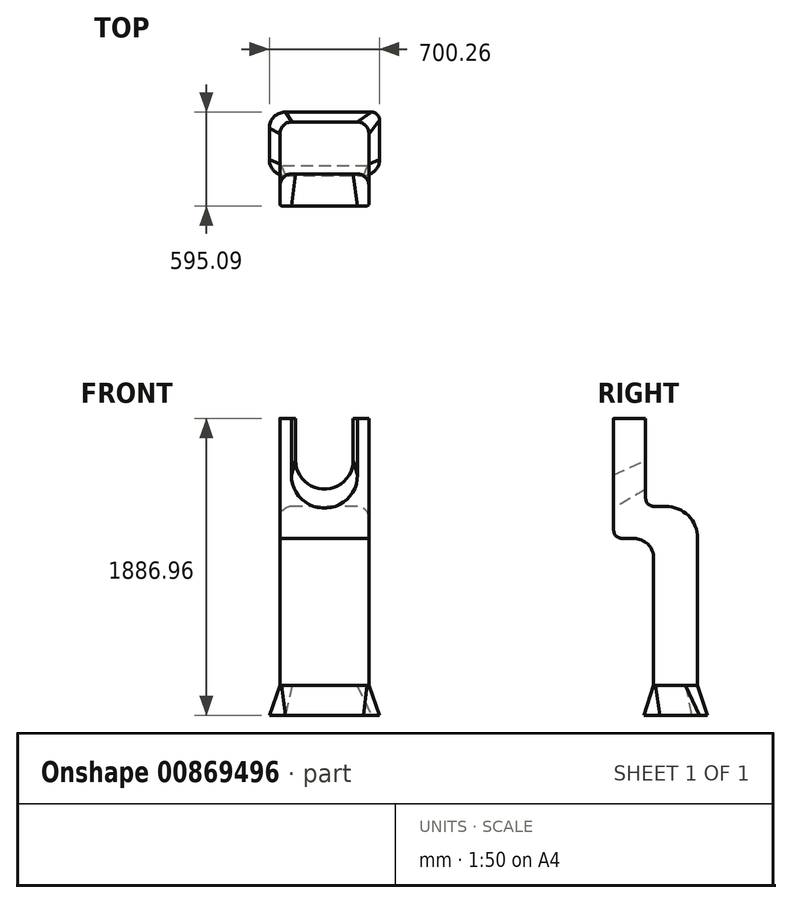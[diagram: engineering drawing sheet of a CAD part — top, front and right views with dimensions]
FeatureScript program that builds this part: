
annotation { "Feature Type Name" : "Feature", "Feature Type Description" : "" }
export const myFeature = defineFeature(function(context is Context, id is Id, definition is map)
    precondition{}
    {
        {
            var Q0;
            Q0=qCreatedBy(makeId("Right.planeOp"),FACE);
            var sketch = newSketch(context, id + "F0", { "sketchPlane" : qUnion([Q0])});
            skLineSegment(sketch, "E0", {"start": v(0, 690.62) * mm, "end": v(0, -1004.83) * mm, "construction": true});
            skSolve(sketch);
        }
        {
            var Q0;
            Q0=qCreatedBy(makeId("Right.planeOp"),FACE);
            var sketch = newSketch(context, id + "F1", { "sketchPlane" : qUnion([Q0])});
            skLineSegment(sketch, "E1", {"start": v(139.7, -1004.83) * mm, "end": v(-139.7, -1004.83) * mm});
            skLineSegment(sketch, "E2", {"start": v(-139.7, -1004.83) * mm, "end": v(-139.7, -198.38) * mm});
            skLineSegment(sketch, "E3", {"start": v(-266.7, -71.38) * mm, "end": v(-342.9, -71.38) * mm});
            skLineSegment(sketch, "E4", {"start": v(-393.7, -20.58) * mm, "end": v(-393.7, 690.62) * mm});
            skLineSegment(sketch, "E5.0", {"start": v(-190.5, 182.62) * mm, "end": v(-190.5, 690.62) * mm});
            skLineSegment(sketch, "E6.0", {"start": v(139.7, -1004.83) * mm, "end": v(139.7, -71.38) * mm});
            skLineSegment(sketch, "E7.0", {"start": v(-63.5, 131.82) * mm, "end": v(-139.7, 131.82) * mm});
            skPoint(sketch, "E8.visualSharp", {"position": v(-393.7, -71.38) * mm});
            skArc(sketch, "E8.filletArc", {"start": v(-393.7, -20.58) * mm, "mid": v(-378.82, -56.5) * mm, "end": v(-342.9, -71.38) * mm});
            skPoint(sketch, "E9.visualSharp", {"position": v(-190.5, 131.82) * mm});
            skArc(sketch, "E9.filletArc", {"start": v(-190.5, 182.62) * mm, "mid": v(-175.62, 146.7) * mm, "end": v(-139.7, 131.82) * mm});
            skPoint(sketch, "E10.visualSharp", {"position": v(-139.7, -71.38) * mm});
            skArc(sketch, "E10.filletArc", {"start": v(-139.7, -198.38) * mm, "mid": v(-176.9, -108.58) * mm, "end": v(-266.7, -71.38) * mm});
            skPoint(sketch, "E11.visualSharp", {"position": v(139.7, 131.82) * mm});
            skArc(sketch, "E11.filletArc", {"start": v(139.7, -71.38) * mm, "mid": v(80.18, 72.3) * mm, "end": v(-63.5, 131.82) * mm});
            skLineSegment(sketch, "E12", {"start": v(-393.7, 690.62) * mm, "end": v(-190.5, 690.62) * mm});
            skSolve(sketch);
        }
        {
            var Q0;
            Q0=makeQuery(id+"F1.imprint","IMPRINT",FACE,{"disambiguationData":[TD([[makeQuery(id+"F1.imprint","IMPRINT",EDGE,{"derivedFrom":sQuery(id+"F1.wireOp",EDGE,"E1")}),-1.0]])]});
            extrude(context, id + "F2", {"entities" : qUnion([Q0]), "depth" : 282.57 * mm, "offsetDistance" : 25.4 * mm, "hasSecondDirection" : true, "secondDirectionOppositeDirection" : true, "secondDirectionDepth" : 282.57 * mm});
        }
        {
            var Q0;
            Q0=qCreatedBy(makeId("Front.planeOp"),FACE);
            cPlane(context, id + "F3", {"entities" : qUnion([Q0]), "cplaneType" : CPlaneType.OFFSET, "offset" : 525.78 * mm, "width" : 152.4 * mm, "height" : 152.4 * mm});
        }
        {
            var Q0;
            Q0=qCreatedBy(makeId("Front.planeOp"),FACE);
            cPlane(context, id + "F4", {"entities" : qUnion([Q0]), "cplaneType" : CPlaneType.OFFSET, "offset" : 154.94 * mm, "width" : 152.4 * mm, "height" : 152.4 * mm});
        }
        {
            var Q0;
            Q0=qCreatedBy(id+"F4.planeOp",FACE);
            var sketch = newSketch(context, id + "F5", { "sketchPlane" : qUnion([Q0])});
            skArc(sketch, "E13", {"start": v(-177.8, 439.13) * mm, "mid": v(0, 261.33) * mm, "end": v(177.8, 439.13) * mm});
            skLineSegment(sketch, "E14", {"start": v(-177.8, 439.13) * mm, "end": v(-177.8, 864.72) * mm});
            skLineSegment(sketch, "E15", {"start": v(177.8, 439.13) * mm, "end": v(177.8, 864.72) * mm});
            skLineSegment(sketch, "E16", {"start": v(-177.8, 864.72) * mm, "end": v(177.8, 864.72) * mm});
            skSolve(sketch);
        }
        {
            var Q0;
            Q0=qCreatedBy(id+"F3.planeOp",FACE);
            var sketch = newSketch(context, id + "F6", { "sketchPlane" : qUnion([Q0])});
            skArc(sketch, "E17", {"start": v(-228.6, 270.81) * mm, "mid": v(0, 42.21) * mm, "end": v(228.6, 270.81) * mm});
            skLineSegment(sketch, "E18", {"start": v(-228.6, 270.81) * mm, "end": v(-228.6, 1000.47) * mm});
            skLineSegment(sketch, "E19", {"start": v(228.6, 270.81) * mm, "end": v(228.6, 1000.47) * mm});
            skLineSegment(sketch, "E20", {"start": v(-228.6, 1000.47) * mm, "end": v(228.6, 1000.47) * mm});
            skSolve(sketch);
        }
        {
            var Q1;
            Q1=makeQuery(id+"F6.imprint","IMPRINT",FACE,{"disambiguationData":[TD([[makeQuery(id+"F6.imprint","IMPRINT",EDGE,{"derivedFrom":sQuery(id+"F6.wireOp",EDGE,"E17")}),1.0]])]});
            var Q2;
            Q2=makeQuery(id+"F5.imprint","IMPRINT",FACE,{"disambiguationData":[TD([[makeQuery(id+"F5.imprint","IMPRINT",EDGE,{"derivedFrom":sQuery(id+"F5.wireOp",EDGE,"E13")}),1.0]])]});
            loft(context, id + "F7", {"operationType" : NewBodyOperationType.REMOVE, "sheetProfilesArray" : [{ "sheetProfileEntities" : qUnion([Q1]) }, { "sheetProfileEntities" : qUnion([Q2]) }]});
        }
        {
            var Q0;
            Q0=makeQuery(id+"F2.opExtrude","CAP_EDGE",EDGE,{"disambiguationData":[OSD([sQuery(id+"F1.wireOp",EDGE,"E4")])],"isStart":true});
            var Q1;
            Q1=makeQuery(id+"F2.opExtrude","CAP_EDGE",EDGE,{"disambiguationData":[OSD([sQuery(id+"F1.wireOp",EDGE,"E4")])],"isStart":false});
            fillet(context, id + "F8", {"entities" : qUnion([Q0, Q1]), "radius" : 11.43 * mm, "tangentPropagation" : true, "allowEdgeOverflow" : false});
        }
        {
            var Q0;
            Q0=makeQuery(id+"F2.opExtrude","CAP_EDGE",EDGE,{"disambiguationData":[OSD([sQuery(id+"F1.wireOp",EDGE,"E5.0")])],"isStart":true});
            var Q1;
            Q1=makeQuery(id+"F2.opExtrude","CAP_EDGE",EDGE,{"disambiguationData":[OSD([sQuery(id+"F1.wireOp",EDGE,"E5.0")])],"isStart":false});
            fillet(context, id + "F9", {"entities" : qUnion([Q0, Q1]), "radius" : 76.2 * mm, "tangentPropagation" : true, "allowEdgeOverflow" : false});
        }
        {
            var Q0;
            Q0=qCreatedBy(makeId("Top.planeOp"),FACE);
            cPlane(context, id + "F10", {"entities" : qUnion([Q0]), "cplaneType" : CPlaneType.OFFSET, "offset" : 1196.34 * mm, "oppositeDirection" : true, "width" : 152.4 * mm, "height" : 152.4 * mm});
        }
        {
            var Q0;
            Q0=qCreatedBy(id+"F10.planeOp",FACE);
            var sketch = newSketch(context, id + "F11", { "sketchPlane" : qUnion([Q0])});
            skLineSegment(sketch, "E21.bottom", {"start": v(-248.53, -201.4) * mm, "end": v(248.53, -201.4) * mm});
            skLineSegment(sketch, "E21.top", {"start": v(-248.53, 201.4) * mm, "end": v(299.33, 201.4) * mm});
            skLineSegment(sketch, "E21.left", {"start": v(-350.13, -99.8) * mm, "end": v(-350.13, 99.8) * mm});
            skLineSegment(sketch, "E21.right", {"start": v(350.13, -99.8) * mm, "end": v(350.13, 150.6) * mm});
            skPoint(sketch, "E21.middle", {"position": v(0, 0) * mm});
            skPoint(sketch, "E22.visualSharp", {"position": v(-350.13, -201.4) * mm});
            skArc(sketch, "E22.filletArc", {"start": v(-350.13, -99.8) * mm, "mid": v(-320.37, -171.63) * mm, "end": v(-248.53, -201.4) * mm});
            skPoint(sketch, "E23.visualSharp", {"position": v(-350.13, 201.4) * mm});
            skArc(sketch, "E23.filletArc", {"start": v(-248.53, 201.4) * mm, "mid": v(-320.37, 171.63) * mm, "end": v(-350.13, 99.8) * mm});
            skPoint(sketch, "E24.visualSharp", {"position": v(350.13, 201.4) * mm});
            skArc(sketch, "E24.filletArc", {"start": v(350.13, 150.6) * mm, "mid": v(335.25, 186.51) * mm, "end": v(299.33, 201.4) * mm});
            skPoint(sketch, "E25.visualSharp", {"position": v(350.13, -201.4) * mm});
            skArc(sketch, "E25.filletArc", {"start": v(248.53, -201.4) * mm, "mid": v(320.37, -171.63) * mm, "end": v(350.13, -99.8) * mm});
            skSolve(sketch);
        }
        {
            var Q1;
            Q1=makeQuery(id+"F2.opExtrude","SWEPT_FACE",FACE,{"disambiguationData":[OSD([sQuery(id+"F1.wireOp",EDGE,"E1")])]});
            var Q2;
            Q2=makeQuery(id+"F11.imprint","IMPRINT",FACE,{"disambiguationData":[TD([[makeQuery(id+"F11.imprint","IMPRINT",EDGE,{"derivedFrom":sQuery(id+"F11.wireOp",EDGE,"E21.bottom")}),1.0]])]});
            loft(context, id + "F12", {"sheetProfilesArray" : [{ "sheetProfileEntities" : qUnion([Q1]) }, { "sheetProfileEntities" : qUnion([Q2]) }]});
        }
    });
